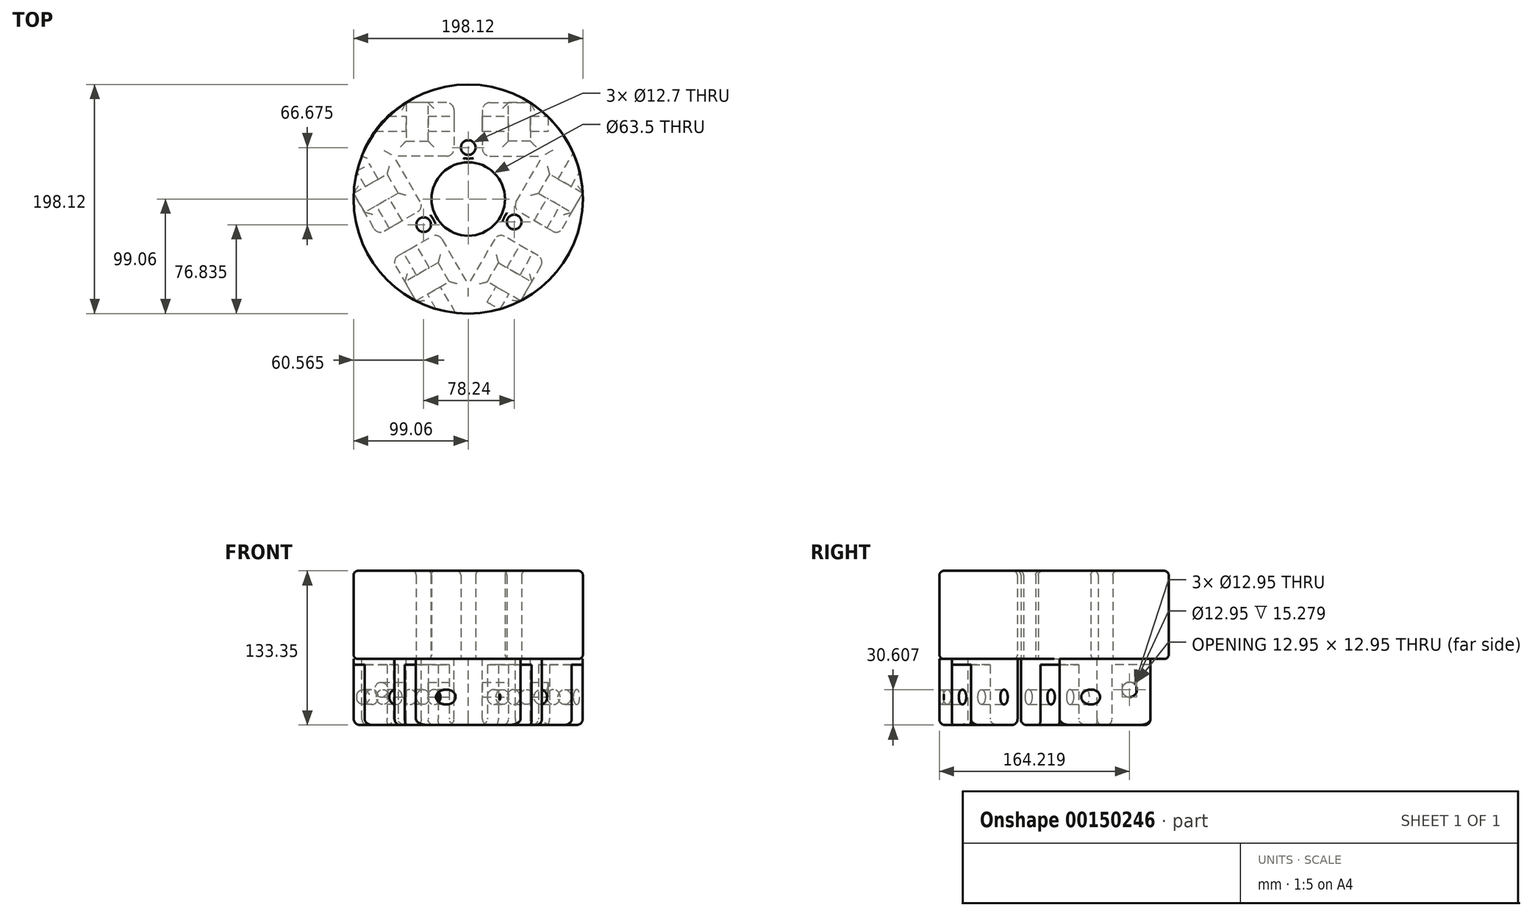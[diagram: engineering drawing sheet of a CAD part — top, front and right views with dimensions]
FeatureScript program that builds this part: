
annotation { "Feature Type Name" : "Feature", "Feature Type Description" : "" }
export const myFeature = defineFeature(function(context is Context, id is Id, definition is map)
    precondition{}
    {
        {
            var Q0;
            Q0=qCreatedBy(makeId("Top.planeOp"),FACE);
            var sketch = newSketch(context, id + "F0", { "sketchPlane" : qUnion([Q0])});
            skCircle(sketch, "E0", {"center": v(0, 0) * mm, "radius": 99.06 * mm});
            skCircle(sketch, "E1", {"center": v(0, 0) * mm, "radius": 31.75 * mm});
            skCircle(sketch, "E2", {"center": v(0, 0) * mm, "radius": 60.33 * mm});
            skCircle(sketch, "E3", {"center": v(0, 44.45) * mm, "radius": 6.35 * mm});
            skCircle(sketch, "E4.1.0", {"center": v(-38.5, -22.22) * mm, "radius": 6.35 * mm});
            skCircle(sketch, "E4.2.0", {"center": v(39.75, -19.9) * mm, "radius": 6.35 * mm});
            skPoint(sketch, "E5.0.midPoint", {"position": v(70.4, -42.12) * mm});
            skPoint(sketch, "E6.orphan", {"position": v(-140.8, 84.25) * mm});
            skPoint(sketch, "E7.orphan", {"position": v(-2.56, -164.06) * mm});
            skPoint(sketch, "E8.orphan", {"position": v(143.36, 79.81) * mm});
            skSolve(sketch);
        }
        {
            var Q0;
            Q0 = qSketchRegion(id + "F0", true);
            var Q1;
            Q1=makeQuery(id+"F0.imprint","IMPRINT",FACE,{"disambiguationData":[TD([[makeQuery(id+"F0.imprint","IMPRINT",EDGE,{"derivedFrom":sQuery(id+"F0.wireOp",EDGE,"E1")}),-1.0]])]});
            extrude(context, id + "F1", {"entities" : qUnion([Q0, Q1]), "depth" : 76.2 * mm});
        }
        {
            var Q0;
            Q0=qCreatedBy(makeId("Top.planeOp"),FACE);
            var sketch = newSketch(context, id + "F2", { "sketchPlane" : qUnion([Q0])});
            skLineSegment(sketch, "E9.top", {"start": v(-18.64, 37.1) * mm, "end": v(-91.85, 37.1) * mm});
            skLineSegment(sketch, "E9.left", {"start": v(-12.29, 76.88) * mm, "end": v(-12.29, 43.44) * mm});
            skPoint(sketch, "E10.1.start.orphan", {"position": v(142.68, 82.37) * mm});
            skPoint(sketch, "E11.orphan", {"position": v(-142.68, 82.37) * mm});
            skLineSegment(sketch, "E12", {"start": v(-18.64, 83.23) * mm, "end": v(-53.71, 83.23) * mm});
            skPoint(sketch, "E13.visualSharp", {"position": v(-12.29, 37.1) * mm});
            skArc(sketch, "E13.filletArc", {"start": v(-18.64, 37.1) * mm, "mid": v(-14.15, 38.95) * mm, "end": v(-12.29, 43.44) * mm});
            skPoint(sketch, "E14.visualSharp", {"position": v(-12.29, 83.23) * mm});
            skArc(sketch, "E14.filletArc", {"start": v(-12.29, 76.88) * mm, "mid": v(-14.15, 81.37) * mm, "end": v(-18.64, 83.23) * mm});
            skLineSegment(sketch, "E15.MirrorCS", {"start": v(18.64, 37.1) * mm, "end": v(91.85, 37.1) * mm});
            skArc(sketch, "E16.MirrorCS", {"start": v(12.29, 76.88) * mm, "mid": v(14.15, 81.37) * mm, "end": v(18.64, 83.23) * mm});
            skArc(sketch, "E17.MirrorCS", {"start": v(18.64, 37.1) * mm, "mid": v(14.15, 38.95) * mm, "end": v(12.29, 43.44) * mm});
            skLineSegment(sketch, "E18.MirrorCS", {"start": v(18.64, 83.23) * mm, "end": v(53.71, 83.23) * mm});
            skLineSegment(sketch, "E19.MirrorCS", {"start": v(12.29, 76.88) * mm, "end": v(12.29, 43.44) * mm});
            skPoint(sketch, "E20.MirrorP", {"position": v(12.29, 83.23) * mm});
            skPoint(sketch, "E21.MirrorP", {"position": v(12.29, 37.1) * mm});
            skPoint(sketch, "E22.1.0", {"position": v(-65.94, -52.26) * mm});
            skLineSegment(sketch, "E22.1.1", {"start": v(-41.44, -2.4) * mm, "end": v(-78.05, 61) * mm});
            skLineSegment(sketch, "E22.1.2", {"start": v(-81.4, -25.48) * mm, "end": v(-98.94, 4.9) * mm});
            skLineSegment(sketch, "E22.1.3", {"start": v(-72.73, -27.8) * mm, "end": v(-43.77, -11.08) * mm});
            skPoint(sketch, "E22.1.4", {"position": v(-25.98, -29.19) * mm});
            skLineSegment(sketch, "E22.1.5", {"start": v(-60.44, -49.08) * mm, "end": v(-31.48, -32.36) * mm});
            skLineSegment(sketch, "E22.1.6", {"start": v(-62.76, -57.76) * mm, "end": v(-45.23, -88.13) * mm});
            skLineSegment(sketch, "E22.1.7", {"start": v(-22.8, -34.69) * mm, "end": v(13.8, -98.1) * mm});
            skPoint(sketch, "E22.1.8", {"position": v(-78.23, -30.97) * mm});
            skPoint(sketch, "E22.1.9", {"position": v(-38.27, -7.9) * mm});
            skPoint(sketch, "E22.1.10", {"position": v(0, -164.75) * mm});
            skArc(sketch, "E22.1.11", {"start": v(-22.8, -34.69) * mm, "mid": v(-26.66, -31.73) * mm, "end": v(-31.48, -32.36) * mm});
            skArc(sketch, "E22.1.12", {"start": v(-41.44, -2.4) * mm, "mid": v(-40.8, -7.22) * mm, "end": v(-43.77, -11.08) * mm});
            skArc(sketch, "E22.1.13", {"start": v(-72.73, -27.8) * mm, "mid": v(-77.55, -28.43) * mm, "end": v(-81.4, -25.48) * mm});
            skArc(sketch, "E22.1.14", {"start": v(-60.44, -49.08) * mm, "mid": v(-63.4, -52.94) * mm, "end": v(-62.76, -57.76) * mm});
            skPoint(sketch, "E22.2.0", {"position": v(78.23, -30.97) * mm});
            skLineSegment(sketch, "E22.2.1", {"start": v(22.8, -34.69) * mm, "end": v(-13.8, -98.1) * mm});
            skLineSegment(sketch, "E22.2.2", {"start": v(62.76, -57.76) * mm, "end": v(45.23, -88.13) * mm});
            skLineSegment(sketch, "E22.2.3", {"start": v(60.44, -49.08) * mm, "end": v(31.48, -32.36) * mm});
            skPoint(sketch, "E22.2.4", {"position": v(38.27, -7.9) * mm});
            skLineSegment(sketch, "E22.2.5", {"start": v(72.73, -27.8) * mm, "end": v(43.77, -11.08) * mm});
            skLineSegment(sketch, "E22.2.6", {"start": v(81.4, -25.48) * mm, "end": v(98.94, 4.9) * mm});
            skLineSegment(sketch, "E22.2.7", {"start": v(41.44, -2.4) * mm, "end": v(78.05, 61) * mm});
            skPoint(sketch, "E22.2.8", {"position": v(65.94, -52.26) * mm});
            skPoint(sketch, "E22.2.9", {"position": v(25.98, -29.19) * mm});
            skArc(sketch, "E22.2.11", {"start": v(41.44, -2.4) * mm, "mid": v(40.8, -7.22) * mm, "end": v(43.77, -11.08) * mm});
            skArc(sketch, "E22.2.12", {"start": v(22.8, -34.69) * mm, "mid": v(26.66, -31.73) * mm, "end": v(31.48, -32.36) * mm});
            skArc(sketch, "E22.2.13", {"start": v(60.44, -49.08) * mm, "mid": v(63.4, -52.94) * mm, "end": v(62.76, -57.76) * mm});
            skArc(sketch, "E22.2.14", {"start": v(72.73, -27.8) * mm, "mid": v(77.55, -28.43) * mm, "end": v(81.4, -25.48) * mm});
            skPoint(sketch, "E22.center", {"position": v(0, 0) * mm});
            skArc(sketch, "E23", {"start": v(-53.71, 83.23) * mm, "mid": v(-76.86, 63.54) * mm, "end": v(-91.85, 37.1) * mm});
            skArc(sketch, "E24", {"start": v(91.85, 37.1) * mm, "mid": v(76.35, 63.11) * mm, "end": v(53.71, 83.23) * mm});
            skArc(sketch, "E25", {"start": v(98.94, 4.9) * mm, "mid": v(92.83, 34.57) * mm, "end": v(78.05, 61) * mm});
            skArc(sketch, "E26", {"start": v(-78.05, 61) * mm, "mid": v(-92.83, 34.57) * mm, "end": v(-98.94, 4.9) * mm});
            skArc(sketch, "E27", {"start": v(-45.23, -88.13) * mm, "mid": v(-16.48, -97.68) * mm, "end": v(13.8, -98.1) * mm});
            skArc(sketch, "E28", {"start": v(-13.8, -98.1) * mm, "mid": v(16.48, -97.68) * mm, "end": v(45.23, -88.13) * mm});
            skSolve(sketch);
        }
        {
            var Q0;
            Q0 = qSketchRegion(id + "F2", true);
            extrude(context, id + "F3", {"entities" : qUnion([Q0]), "oppositeDirection" : true, "depth" : 57.15 * mm});
        }
        {
            var Q0;
            Q0=makeQuery(id+"F3.opExtrude","SWEPT_FACE",FACE,{"disambiguationData":[OSD([sQuery(id+"F2.wireOp",EDGE,"E22.1.5")])]});
            var sketch = newSketch(context, id + "F4", { "sketchPlane" : qUnion([Q0])});
            skCircle(sketch, "E29", {"center": v(65.16, -32.9) * mm, "radius": 6.48 * mm});
            skSolve(sketch);
        }
        {
            var Q0;
            Q0 = qSketchRegion(id + "F4", true);
            extrude(context, id + "F5", {"entities" : qUnion([Q0]), "operationType" : NewBodyOperationType.REMOVE, "endBound" : BoundingType.SYMMETRIC, "oppositeDirection" : true, "depth" : 162.56 * mm});
        }
        {
            var Q0;
            Q0=makeQuery(id+"F3.opExtrude","SWEPT_FACE",FACE,{"disambiguationData":[OSD([sQuery(id+"F2.wireOp",EDGE,"E9.left")])]});
            var sketch = newSketch(context, id + "F6", { "sketchPlane" : qUnion([Q0])});
            skCircle(sketch, "E30", {"center": v(65.16, -26.54) * mm, "radius": 6.48 * mm});
            skSolve(sketch);
        }
        {
            var Q0;
            Q0 = qSketchRegion(id + "F6", true);
            extrude(context, id + "F7", {"entities" : qUnion([Q0]), "operationType" : NewBodyOperationType.REMOVE, "endBound" : BoundingType.SYMMETRIC, "oppositeDirection" : true, "depth" : 162.56 * mm});
        }
        {
            var Q0;
            Q0=makeQuery(id+"F3.opExtrude","SWEPT_FACE",FACE,{"disambiguationData":[OSD([sQuery(id+"F2.wireOp",EDGE,"E22.2.5")])]});
            var sketch = newSketch(context, id + "F8", { "sketchPlane" : qUnion([Q0])});
            skCircle(sketch, "E31", {"center": v(65.16, -32.9) * mm, "radius": 6.48 * mm});
            skSolve(sketch);
        }
        {
            var Q0;
            Q0 = qSketchRegion(id + "F8", true);
            extrude(context, id + "F9", {"entities" : qUnion([Q0]), "operationType" : NewBodyOperationType.REMOVE, "endBound" : BoundingType.SYMMETRIC, "depth" : 162.56 * mm});
        }
        {
            var Q0;
            Q0=makeQuery(id+"F3.opExtrude","CAP_FACE",FACE,{"disambiguationData":[OSD([sQuery(id+"F2.wireOp",EDGE,"E22.1.5"),sQuery(id+"F2.wireOp",EDGE,"E22.1.6"),sQuery(id+"F2.wireOp",EDGE,"E22.1.7"),sQuery(id+"F2.wireOp",EDGE,"E22.1.11"),sQuery(id+"F2.wireOp",EDGE,"E22.1.14"),sQuery(id+"F2.wireOp",EDGE,"E22.2.1"),sQuery(id+"F2.wireOp",EDGE,"E22.2.2"),sQuery(id+"F2.wireOp",EDGE,"E22.2.3"),sQuery(id+"F2.wireOp",EDGE,"E22.2.12"),sQuery(id+"F2.wireOp",EDGE,"E22.2.13"),sQuery(id+"F2.wireOp",EDGE,"E27"),sQuery(id+"F2.wireOp",EDGE,"E28")])],"isStart":false});
            var sketch = newSketch(context, id + "F10", { "sketchPlane" : qUnion([Q0])});
            skLineSegment(sketch, "E32", {"start": v(-54.75, 71.64) * mm, "end": v(-26.02, 55.04) * mm});
            skLineSegment(sketch, "E33", {"start": v(-26.02, 55.04) * mm, "end": v(-16.5, 71.54) * mm});
            skLineSegment(sketch, "E34", {"start": v(-16.5, 71.54) * mm, "end": v(-45.23, 88.13) * mm});
            skLineSegment(sketch, "E35.MirrorCS", {"start": v(54.75, 71.64) * mm, "end": v(26.02, 55.04) * mm});
            skLineSegment(sketch, "E36.MirrorCS", {"start": v(26.02, 55.04) * mm, "end": v(16.5, 71.54) * mm});
            skLineSegment(sketch, "E37.MirrorCS", {"start": v(16.5, 71.54) * mm, "end": v(45.23, 88.13) * mm});
            skLineSegment(sketch, "E38", {"start": v(-54.75, 71.64) * mm, "end": v(-45.23, 88.13) * mm});
            skLineSegment(sketch, "E39", {"start": v(45.23, 88.13) * mm, "end": v(54.75, 71.64) * mm});
            skLineSegment(sketch, "E40.1.0", {"start": v(-70.2, -21.49) * mm, "end": v(-98.94, -4.9) * mm});
            skLineSegment(sketch, "E40.1.1", {"start": v(-98.94, -4.9) * mm, "end": v(-89.41, 11.6) * mm});
            skLineSegment(sketch, "E40.1.2", {"start": v(-34.66, -50.05) * mm, "end": v(-53.71, -50.05) * mm});
            skLineSegment(sketch, "E40.1.3", {"start": v(-53.71, -50.05) * mm, "end": v(-53.71, -83.23) * mm});
            skLineSegment(sketch, "E40.1.4", {"start": v(-89.41, 11.6) * mm, "end": v(-60.68, -5) * mm});
            skLineSegment(sketch, "E40.1.5", {"start": v(-60.68, -5) * mm, "end": v(-70.2, -21.49) * mm});
            skLineSegment(sketch, "E40.1.6", {"start": v(-34.66, -83.23) * mm, "end": v(-34.66, -50.05) * mm});
            skLineSegment(sketch, "E40.1.7", {"start": v(-34.66, -83.23) * mm, "end": v(-53.71, -83.23) * mm});
            skLineSegment(sketch, "E40.1.8", {"start": v(-70.2, -21.49) * mm, "end": v(-98.94, -4.9) * mm});
            skLineSegment(sketch, "E40.1.9", {"start": v(-34.66, -50.05) * mm, "end": v(-53.71, -50.05) * mm});
            skLineSegment(sketch, "E40.1.10", {"start": v(-53.71, -50.05) * mm, "end": v(-53.71, -83.23) * mm});
            skLineSegment(sketch, "E40.1.11", {"start": v(-89.41, 11.6) * mm, "end": v(-60.68, -5) * mm});
            skLineSegment(sketch, "E40.1.12", {"start": v(-60.68, -5) * mm, "end": v(-70.2, -21.49) * mm});
            skLineSegment(sketch, "E40.1.13", {"start": v(-34.66, -83.23) * mm, "end": v(-34.66, -50.05) * mm});
            skLineSegment(sketch, "E40.2.0", {"start": v(53.71, -50.05) * mm, "end": v(53.71, -83.23) * mm});
            skLineSegment(sketch, "E40.2.1", {"start": v(53.71, -83.23) * mm, "end": v(34.66, -83.23) * mm});
            skLineSegment(sketch, "E40.2.2", {"start": v(60.68, -5) * mm, "end": v(70.2, -21.49) * mm});
            skLineSegment(sketch, "E40.2.3", {"start": v(70.2, -21.49) * mm, "end": v(98.94, -4.9) * mm});
            skLineSegment(sketch, "E40.2.4", {"start": v(34.66, -83.23) * mm, "end": v(34.66, -50.05) * mm});
            skLineSegment(sketch, "E40.2.5", {"start": v(34.66, -50.05) * mm, "end": v(53.71, -50.05) * mm});
            skLineSegment(sketch, "E40.2.6", {"start": v(89.41, 11.6) * mm, "end": v(60.68, -5) * mm});
            skLineSegment(sketch, "E40.2.7", {"start": v(89.41, 11.6) * mm, "end": v(98.94, -4.9) * mm});
            skLineSegment(sketch, "E40.2.8", {"start": v(53.71, -50.05) * mm, "end": v(53.71, -83.23) * mm});
            skLineSegment(sketch, "E40.2.9", {"start": v(60.68, -5) * mm, "end": v(70.2, -21.49) * mm});
            skLineSegment(sketch, "E40.2.10", {"start": v(70.2, -21.49) * mm, "end": v(98.94, -4.9) * mm});
            skLineSegment(sketch, "E40.2.11", {"start": v(34.66, -83.23) * mm, "end": v(34.66, -50.05) * mm});
            skLineSegment(sketch, "E40.2.12", {"start": v(34.66, -50.05) * mm, "end": v(53.71, -50.05) * mm});
            skLineSegment(sketch, "E40.2.13", {"start": v(89.41, 11.6) * mm, "end": v(60.68, -5) * mm});
            skPoint(sketch, "E40.center", {"position": v(0, 0) * mm});
            skSolve(sketch);
        }
        {
            var Q0;
            Q0 = qSketchRegion(id + "F10", true);
            extrude(context, id + "F11", {"entities" : qUnion([Q0]), "operationType" : NewBodyOperationType.REMOVE, "oppositeDirection" : true, "depth" : 52.07 * mm, "hasSecondDirection" : true, "secondDirectionOppositeDirection" : false, "secondDirectionDepth" : 25.4 * mm});
        }
        {
            var Q0;
            Q0=makeQuery(id+"F3.opExtrude","CAP_FACE",FACE,{"disambiguationData":[OSD([sQuery(id+"F2.wireOp",EDGE,"E15.MirrorCS"),sQuery(id+"F2.wireOp",EDGE,"E16.MirrorCS"),sQuery(id+"F2.wireOp",EDGE,"E17.MirrorCS"),sQuery(id+"F2.wireOp",EDGE,"E18.MirrorCS"),sQuery(id+"F2.wireOp",EDGE,"E19.MirrorCS"),sQuery(id+"F2.wireOp",EDGE,"E22.2.5"),sQuery(id+"F2.wireOp",EDGE,"E22.2.6"),sQuery(id+"F2.wireOp",EDGE,"E22.2.7"),sQuery(id+"F2.wireOp",EDGE,"E22.2.11"),sQuery(id+"F2.wireOp",EDGE,"E22.2.14"),sQuery(id+"F2.wireOp",EDGE,"E24"),sQuery(id+"F2.wireOp",EDGE,"E25")])],"isStart":false});
            var Q1;
            Q1=makeQuery(id+"F3.opExtrude","CAP_FACE",FACE,{"disambiguationData":[OSD([sQuery(id+"F2.wireOp",EDGE,"E9.top"),sQuery(id+"F2.wireOp",EDGE,"E9.left"),sQuery(id+"F2.wireOp",EDGE,"E12"),sQuery(id+"F2.wireOp",EDGE,"E13.filletArc"),sQuery(id+"F2.wireOp",EDGE,"E14.filletArc"),sQuery(id+"F2.wireOp",EDGE,"E22.1.1"),sQuery(id+"F2.wireOp",EDGE,"E22.1.2"),sQuery(id+"F2.wireOp",EDGE,"E22.1.3"),sQuery(id+"F2.wireOp",EDGE,"E22.1.12"),sQuery(id+"F2.wireOp",EDGE,"E22.1.13"),sQuery(id+"F2.wireOp",EDGE,"E23"),sQuery(id+"F2.wireOp",EDGE,"E26")])],"isStart":false});
            var Q2;
            Q2=makeQuery(id+"F3.opExtrude","CAP_FACE",FACE,{"disambiguationData":[OSD([sQuery(id+"F2.wireOp",EDGE,"E22.1.5"),sQuery(id+"F2.wireOp",EDGE,"E22.1.6"),sQuery(id+"F2.wireOp",EDGE,"E22.1.7"),sQuery(id+"F2.wireOp",EDGE,"E22.1.11"),sQuery(id+"F2.wireOp",EDGE,"E22.1.14"),sQuery(id+"F2.wireOp",EDGE,"E22.2.1"),sQuery(id+"F2.wireOp",EDGE,"E22.2.2"),sQuery(id+"F2.wireOp",EDGE,"E22.2.3"),sQuery(id+"F2.wireOp",EDGE,"E22.2.12"),sQuery(id+"F2.wireOp",EDGE,"E22.2.13"),sQuery(id+"F2.wireOp",EDGE,"E27"),sQuery(id+"F2.wireOp",EDGE,"E28")])],"isStart":false});
            fillet(context, id + "F12", {"entities" : qUnion([Q0, Q1, Q2]), "radius" : 5.08 * mm, "tangentPropagation" : true, "allowEdgeOverflow" : false});
        }
        {
            var Q0;
            Q0=makeQuery(id+"F1.opExtrude","CAP_FACE",FACE,{"disambiguationData":[OSD([sQuery(id+"F0.wireOp",EDGE,"E0"),sQuery(id+"F0.wireOp",EDGE,"E1"),sQuery(id+"F0.wireOp",EDGE,"E3"),sQuery(id+"F0.wireOp",EDGE,"E4.1.0"),sQuery(id+"F0.wireOp",EDGE,"E4.2.0")])],"isStart":false});
            var Q1;
            Q1=makeQuery(id+"F1.opExtrude","SWEPT_FACE",FACE,{"disambiguationData":[OSD([sQuery(id+"F0.wireOp",EDGE,"E0")])]});
            var Q2;
            Q2=makeQuery(id+"F1.opExtrude","SWEPT_FACE",FACE,{"disambiguationData":[OSD([sQuery(id+"F0.wireOp",EDGE,"E1")])]});
            fillet(context, id + "F13", {"entities" : qUnion([Q0, Q1, Q2]), "radius" : 3.8 * mm, "tangentPropagation" : true, "allowEdgeOverflow" : false});
        }
    });
